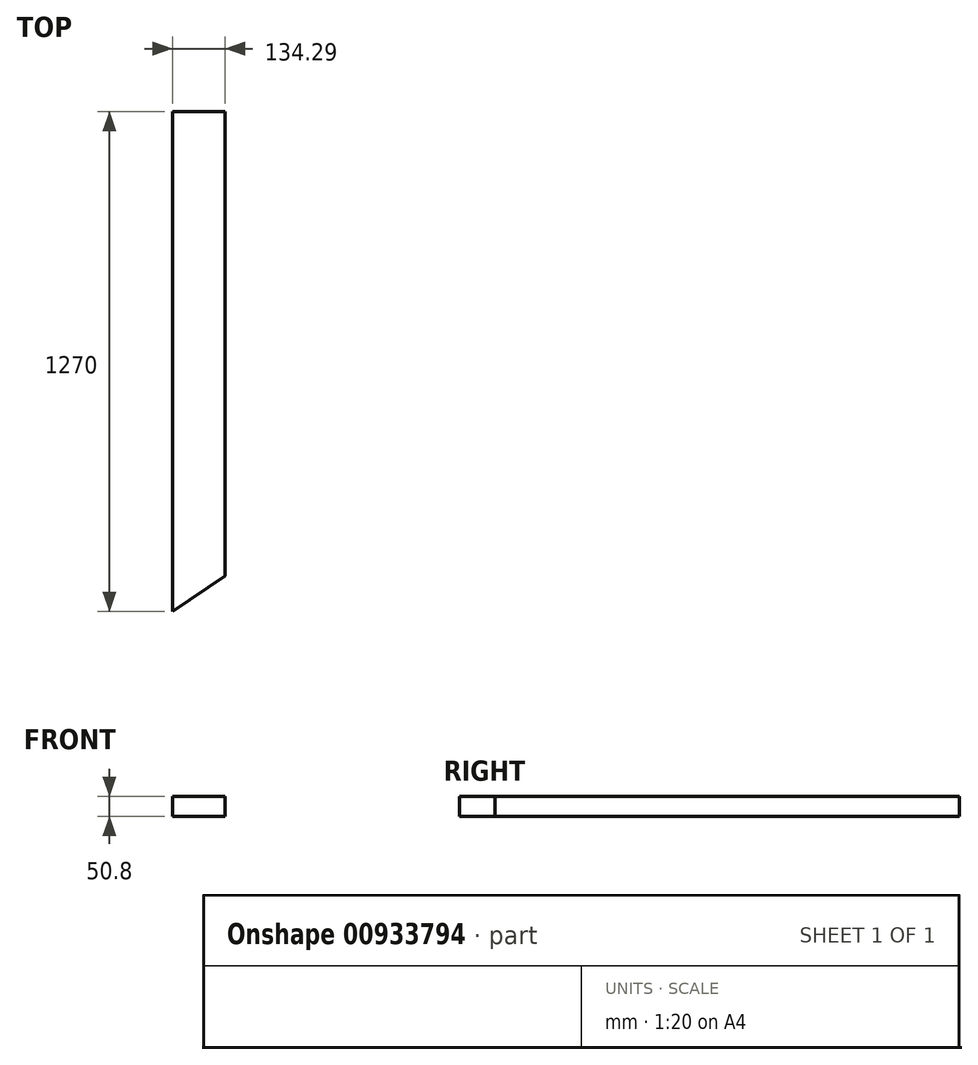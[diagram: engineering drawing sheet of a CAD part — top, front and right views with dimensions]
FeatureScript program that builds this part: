
annotation { "Feature Type Name" : "Feature", "Feature Type Description" : "" }
export const myFeature = defineFeature(function(context is Context, id is Id, definition is map)
    precondition{}
    {
        {
            var Q0;
            Q0=qCreatedBy(makeId("Top.planeOp"),FACE);
            var sketch = newSketch(context, id + "F0", { "sketchPlane" : qUnion([Q0])});
            skLineSegment(sketch, "E0", {"start": v(-134.3, -73.32) * mm, "end": v(-134.3, 1196.68) * mm});
            skLineSegment(sketch, "E1", {"start": v(-134.3, 1196.68) * mm, "end": v(0, 1196.68) * mm});
            skLineSegment(sketch, "E2", {"start": v(0, 1196.68) * mm, "end": v(0, 16.99) * mm});
            skLineSegment(sketch, "E3", {"start": v(0, 16.99) * mm, "end": v(-134.3, -73.32) * mm});
            skSolve(sketch);
        }
        {
            var Q0;
            Q0=makeQuery(id+"F0.imprint","IMPRINT",FACE,{"disambiguationData":[TD([[makeQuery(id+"F0.imprint","IMPRINT",EDGE,{"derivedFrom":sQuery(id+"F0.wireOp",EDGE,"E0")}),-1.0]])]});
            extrude(context, id + "F1", {"entities" : qUnion([Q0]), "depth" : 50.8 * mm, "offsetDistance" : 25.4 * mm});
        }
    });
